# Revit family: Camera-Security-Panasonic-Super_Dynamic-H265_AI_Engine-Vandal_Resistant-Dome-Network-S2236LSeriesX
name_source: partatom
category: Security Devices
units: mm (PartAtom-declared; Revit-internal decimal feet)

## family parameters
Cut with Voids When Loaded = No
Host = Face
Maintain Annotation Orientation = No
OmniClass Number = 23.85.10.14.11
OmniClass Title = Cameras
Part Type = Normal
Room Calculation Point = No
Round Connector Dimension = Use Diameter
Shared = No

## types (1)
- WV-S2236L
    Alarm Input Or Output Specification = ALARM IN 1 (Black & white input, Auto time adjustment input) (x1), ALARM IN 2 (ALARM OUT) (x1), ALARM IN 3 (AUX OUT) (x1)
    Angle Of View = 114
    Audio In = ø3.5 mm stereo mini jack
    Audio Out = ø3.5 mm stereo mini jack (monaural output)
    Communication Ports = 10Base-T / 100Base-TX, RJ45 connector
    Date Last Modified = 2021/04/09
    Day Or Night = Yes
    Default Elevation = 0 "
    Description = Security Camera, Vandal Resistant, H.265 Fixed Dome, Network, Super Dynamic FullHD, AI Engine, WV-S2236L
    Diameter = 5.098 "
    Equipment Abbreviation = SC
    Family Version = 1.0.0
    HFOV Max 169 = 114.00°
    HFOV Max 43 = 82.00°
    HFOV Min 169 = 36.00°
    HFOV Min 43 = 27.00°
    Has POE = Yes
    Height = 4.035 "
    IP Or Analog = IP
    Indoor Or Outdoor = Indoor
    Manufacturer = Panasonic
    Minimum Illumination = 0.007 lx
    Model = WV-S2236L
    Model Disclaimer = Contact Panasonic for more information
    Mounting Positions = Surface Mount or Mount Dependent
    Operational Humidity = 10 to 90 % (no condensation)
    Operational Temperature = -10 °C to +50 °C (14 °F to 122 °F)
    Pan Max = 120.00°
    Pan Min = -240.00°
    Panning Range = -240 to +120
    Part Description = Security Camera, Vandal Resistant, H.265 Fixed Dome, Network, Super Dynamic FullHD, AI Engine, WV-S2236L
    Part Number = WV-S2236L
    Product Documentation Link = https://bizpartner.panasonic.net
    Product Material = Paint - Panasonic -i-Pro White
    Product Page URL = https://security.panasonic.com
    Provide Feedback = https://www.surveymonkey.com
    Regulatory Compliance = UL (UL60950-1), c-UL (CSA C22.2 No.60950-1), CE, IEC60950-1, FCC (Part15 ClassA), ICES003 ClassA, EN55032 ClassB, EN55035
    Shock Resistance = IK10 (IEC 62262)
    Storage Temperature = -10 °C to +50 °C (14 °F to 122 °F)
    Tilt Max = 85.00°
    Tilt Min = -30.00°
    Tilting Range = -30 to +85
    URL = http://security.panasonic.com
    VFOV Max 169 = 60.00°
    VFOV Max 43 = 60.00°
    VFOV Min 169 = 20.00°
    VFOV Min 43 = 20.00°
    Vandal Resistant = Yes
    Weight = 1.26 lb
    Wide Dynamic Range = Yes
    Yaw Max = 100.00°
    Yaw Min = -100.00°
    Yawing Range = -100 to +100
    z Base Height = 2.118 "
    z Base Radius = 2.549 "
    z Camera Resolution Type = 1
    z Camera Type = 21362
    z Const Pan Handle Length = 19.488 "
    z Const Tilt Base Length = 9.843 "
    z Const Tilt Base2 Length = 19.685 "
    z Const Tilt Handle Length = 11.811 "
    z Const Yaw Base Length = 10.236 "
    z Const Yaw Base2 Length = 17.323 "
    z Const Yaw Handle Length = 9.252 "
    z Dome Material = Glass - Panasonic - Smoked
    z Type = 2
    z VV Face Radius = 4.626 "
    z VV Origin Height Offset = 0.303 "
    z VV Viewpoint Depth Max = 1.283 "
    z VV Viewpoint Depth Min = 1.283 "
    z Zero = 0 "

## geometry (parser evidence)
native form markers: Blend x2, Sweep x5
no freeform markers — native parametric forms only
